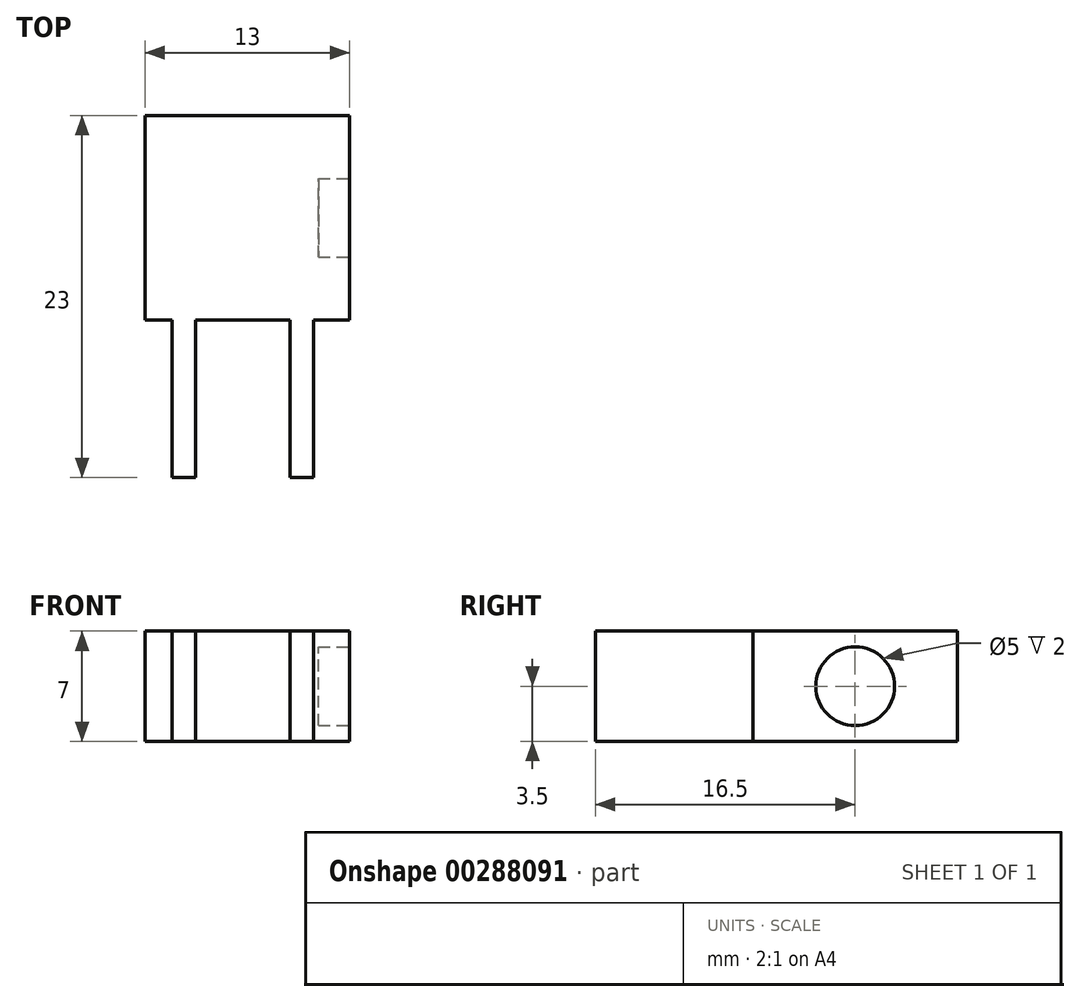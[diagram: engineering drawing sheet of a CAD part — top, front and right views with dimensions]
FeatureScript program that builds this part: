
annotation { "Feature Type Name" : "Feature", "Feature Type Description" : "" }
export const myFeature = defineFeature(function(context is Context, id is Id, definition is map)
    precondition{}
    {
        {
            var Q0;
            Q0=qCreatedBy(makeId("Top.planeOp"),FACE);
            var sketch = newSketch(context, id + "F0", { "sketchPlane" : qUnion([Q0])});
            skLineSegment(sketch, "E0.bottom", {"start": v(0, 0) * mm, "end": v(13, 0) * mm});
            skLineSegment(sketch, "E0.top", {"start": v(0, -13) * mm, "end": v(13, -13) * mm});
            skLineSegment(sketch, "E0.left", {"start": v(0, 0) * mm, "end": v(0, -13) * mm});
            skLineSegment(sketch, "E0.right", {"start": v(13, 0) * mm, "end": v(13, -13) * mm});
            skLineSegment(sketch, "E1", {"start": v(1.7, -13) * mm, "end": v(1.7, -23) * mm});
            skLineSegment(sketch, "E2", {"start": v(1.7, -23) * mm, "end": v(3.2, -23) * mm});
            skLineSegment(sketch, "E3", {"start": v(3.2, -23) * mm, "end": v(3.2, -13) * mm});
            skLineSegment(sketch, "E4", {"start": v(3.2, -13) * mm, "end": v(9.2, -13) * mm});
            skLineSegment(sketch, "E5", {"start": v(9.2, -13) * mm, "end": v(9.2, -23) * mm});
            skLineSegment(sketch, "E6", {"start": v(9.2, -23) * mm, "end": v(10.7, -23) * mm});
            skLineSegment(sketch, "E7", {"start": v(10.7, -23) * mm, "end": v(10.7, -13) * mm});
            skSolve(sketch);
        }
        {
            var Q0;
            Q0=qSketchRegion(id+"F0",true);
            extrude(context, id + "F1", {"entities" : qUnion([Q0]), "depth" : 7 * mm});
        }
        {
            var Q0;
            Q0=makeQuery(id+"F1.opExtrude","SWEPT_FACE",FACE,{"disambiguationData":[OSD([sQuery(id+"F0.wireOp",EDGE,"E0.right")])]});
            var sketch = newSketch(context, id + "F2", { "sketchPlane" : qUnion([Q0])});
            skCircle(sketch, "E8", {"center": v(-6.5, 3.5) * mm, "radius": 2.5 * mm});
            skSolve(sketch);
        }
        {
            var Q0;
            Q0=qSketchRegion(id+"F2",true);
            extrude(context, id + "F3", {"entities" : qUnion([Q0]), "operationType" : NewBodyOperationType.REMOVE, "oppositeDirection" : true, "depth" : 2 * mm});
        }
    });
